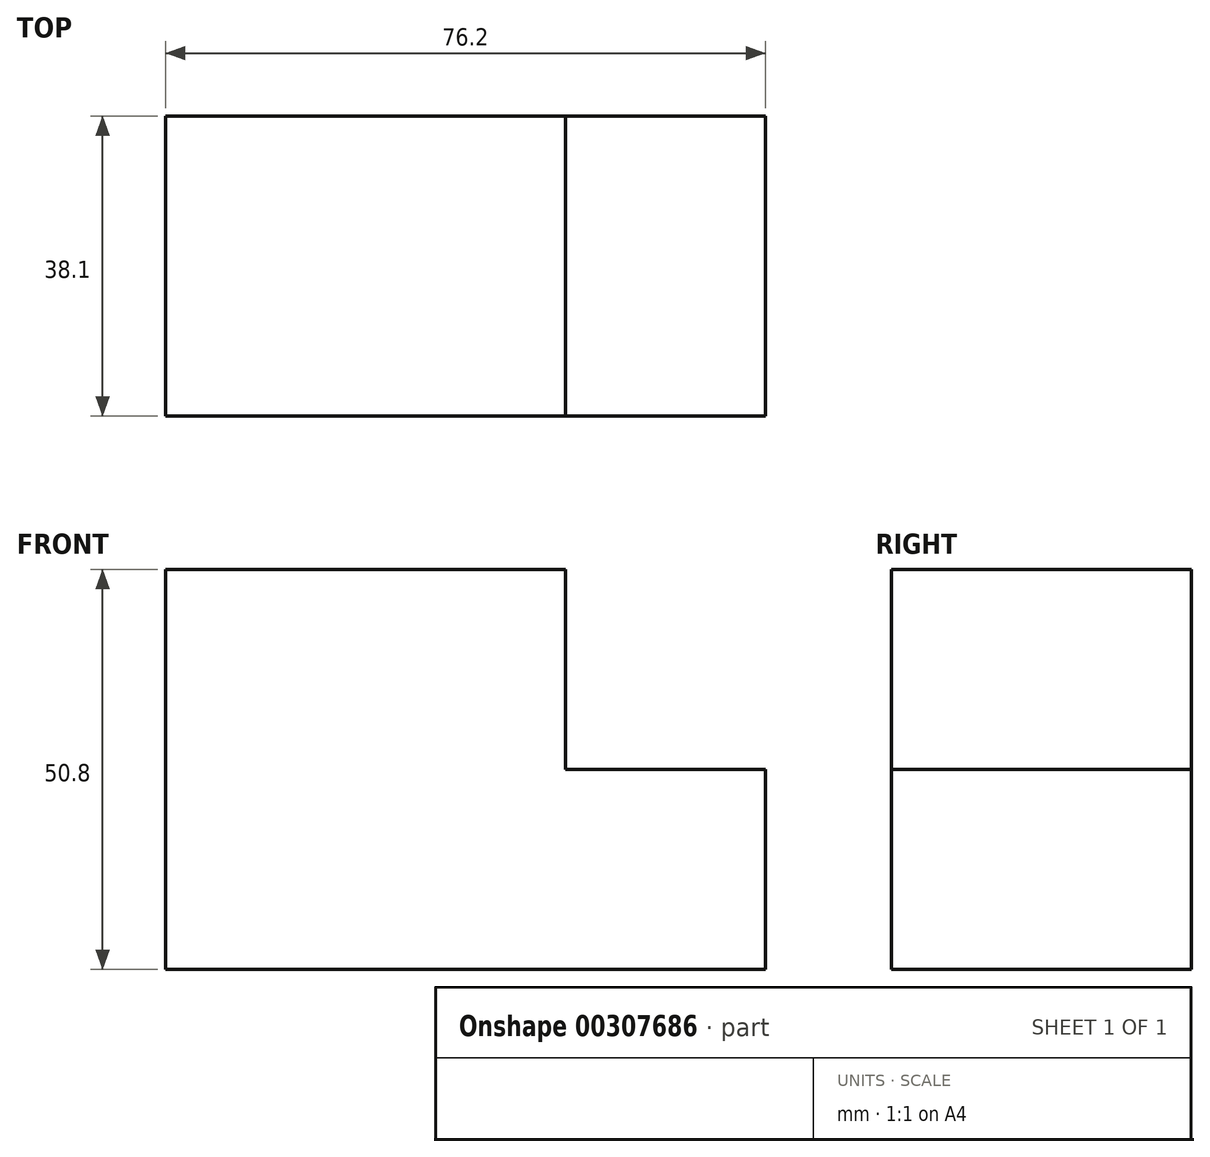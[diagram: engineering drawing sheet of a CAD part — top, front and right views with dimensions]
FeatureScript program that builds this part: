
annotation { "Feature Type Name" : "Feature", "Feature Type Description" : "" }
export const myFeature = defineFeature(function(context is Context, id is Id, definition is map)
    precondition{}
    {
        {
            var Q0;
            Q0=qCreatedBy(makeId("Front.planeOp"),FACE);
            var sketch = newSketch(context, id + "F0", { "sketchPlane" : qUnion([Q0])});
            skLineSegment(sketch, "E0", {"start": v(-33.67, -38.66) * mm, "end": v(42.53, -38.66) * mm});
            skLineSegment(sketch, "E1", {"start": v(42.53, -38.66) * mm, "end": v(42.53, -13.26) * mm});
            skLineSegment(sketch, "E2", {"start": v(42.53, -13.26) * mm, "end": v(17.13, -13.26) * mm});
            skLineSegment(sketch, "E3", {"start": v(17.13, -13.26) * mm, "end": v(17.13, 12.14) * mm});
            skLineSegment(sketch, "E4", {"start": v(17.13, 12.14) * mm, "end": v(-33.67, 12.14) * mm});
            skLineSegment(sketch, "E5", {"start": v(-33.67, 12.14) * mm, "end": v(-33.67, -38.66) * mm});
            skSolve(sketch);
        }
        {
            var Q0;
            Q0=makeQuery(id+"F0.imprint","IMPRINT",FACE,{"disambiguationData":[TD([[makeQuery(id+"F0.imprint","IMPRINT",EDGE,{"derivedFrom":sQuery(id+"F0.wireOp",EDGE,"E0")}),1.0]])]});
            extrude(context, id + "F1", {"entities" : qUnion([Q0]), "depth" : 38.1 * mm});
        }
    });
